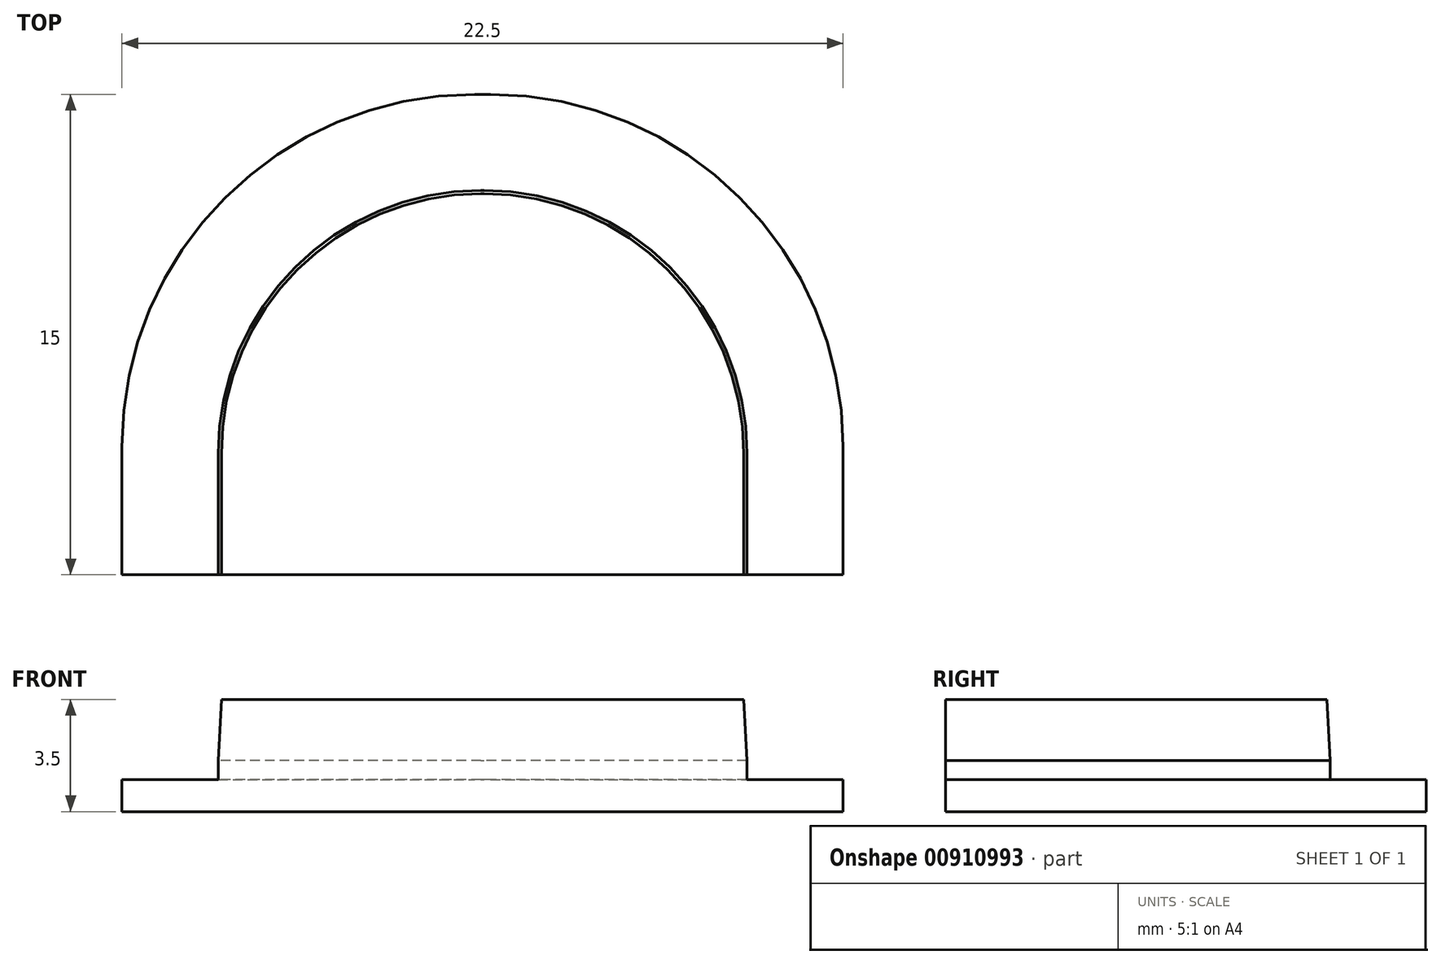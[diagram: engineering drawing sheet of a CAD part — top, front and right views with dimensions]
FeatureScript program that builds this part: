
annotation { "Feature Type Name" : "Feature", "Feature Type Description" : "" }
export const myFeature = defineFeature(function(context is Context, id is Id, definition is map)
    precondition{}
    {
        {
            var Q0;
            Q0=qCreatedBy(makeId("Top.planeOp"),FACE);
            var sketch = newSketch(context, id + "F0", { "sketchPlane" : qUnion([Q0])});
            skLineSegment(sketch, "E0.bottom", {"start": v(0, 0) * mm, "end": v(16.5, 0) * mm});
            skLineSegment(sketch, "E0.top", {"start": v(0, -12) * mm, "end": v(16.5, -12) * mm});
            skLineSegment(sketch, "E0.left", {"start": v(0, 0) * mm, "end": v(0, -12) * mm});
            skLineSegment(sketch, "E0.right", {"start": v(16.5, 0) * mm, "end": v(16.5, -12) * mm});
            skSolve(sketch);
        }
        {
            var Q0;
            Q0 = qSketchRegion(id + "F0", true);
            extrude(context, id + "F1", {"entities" : qUnion([Q0]), "depth" : 2.5 * mm, "offsetDistance" : 25 * mm});
        }
        {
            var Q0;
            Q0=makeQuery(id+"F1.opExtrude","SWEPT_EDGE",EDGE,{"disambiguationData":[OSD([sQuery(id+"F0.wireOp",EDGE,"E0.bottom"),sQuery(id+"F0.wireOp",EDGE,"E0.right")])]});
            var Q1;
            Q1=makeQuery(id+"F1.opExtrude","SWEPT_EDGE",EDGE,{"disambiguationData":[OSD([sQuery(id+"F0.wireOp",EDGE,"E0.bottom"),sQuery(id+"F0.wireOp",EDGE,"E0.left")])]});
            fillet(context, id + "F2", {"entities" : qUnion([Q0, Q1]), "radius" : 8.2 * mm, "tangentPropagation" : true, "allowEdgeOverflow" : false});
        }
        {
            var Q0;
            Q0=makeQuery(id+"F1.opExtrude","CAP_FACE",FACE,{"disambiguationData":[OSD([sQuery(id+"F0.wireOp",EDGE,"E0.bottom"),sQuery(id+"F0.wireOp",EDGE,"E0.top"),sQuery(id+"F0.wireOp",EDGE,"E0.left"),sQuery(id+"F0.wireOp",EDGE,"E0.right")])],"isStart":true});
            var sketch = newSketch(context, id + "F3", { "sketchPlane" : qUnion([Q0])});
            skLineSegment(sketch, "E1.bottom", {"start": v(19.5, 12) * mm, "end": v(-3, 12) * mm});
            skLineSegment(sketch, "E1.top", {"start": v(19.5, -3) * mm, "end": v(-3, -3) * mm});
            skLineSegment(sketch, "E1.left", {"start": v(19.5, 12) * mm, "end": v(19.5, -3) * mm});
            skLineSegment(sketch, "E1.right", {"start": v(-3, 12) * mm, "end": v(-3, -3) * mm});
            skSolve(sketch);
        }
        {
            var Q0;
            Q0 = qSketchRegion(id + "F3", true);
            extrude(context, id + "F4", {"entities" : qUnion([Q0]), "operationType" : NewBodyOperationType.ADD, "depth" : 1 * mm, "offsetDistance" : 25 * mm});
        }
        {
            var Q0;
            Q0=makeQuery(id+"F4.opExtrude","SWEPT_EDGE",EDGE,{"disambiguationData":[OSD([sQuery(id+"F3.wireOp",EDGE,"E1.top"),sQuery(id+"F3.wireOp",EDGE,"E1.left")])]});
            var Q1;
            Q1=makeQuery(id+"F4.opExtrude","SWEPT_EDGE",EDGE,{"disambiguationData":[OSD([sQuery(id+"F3.wireOp",EDGE,"E1.top"),sQuery(id+"F3.wireOp",EDGE,"E1.right")])]});
            fillet(context, id + "F5", {"entities" : qUnion([Q0, Q1]), "radius" : 11 * mm, "tangentPropagation" : true, "allowEdgeOverflow" : false});
        }
        {
            var Q0;
            Q0=makeQuery(id+"F1.opExtrude","CAP_EDGE",EDGE,{"disambiguationData":[OSD([sQuery(id+"F0.wireOp",EDGE,"E0.left")])],"isStart":false});
            var Q1;
            {var subQ0=sQuery(id+"F0.wireOp",EDGE,"E0.left");var subQ1=sQuery(id+"F0.wireOp",EDGE,"E0.bottom");Q1=makeQuery(id+"F2.opFillet","BLEND_EDGE",EDGE,{"blendedFrom":[makeQuery(id+"F1.opExtrude","SWEPT_EDGE",EDGE,{"disambiguationData":[OSD([subQ1,subQ0])]}),makeQuery(id+"F1.opExtrude","CAP_FACE",FACE,{"disambiguationData":[OSD([subQ1,sQuery(id+"F0.wireOp",EDGE,"E0.top"),subQ0,sQuery(id+"F0.wireOp",EDGE,"E0.right")])],"isStart":false})],"blendedInto":[makeQuery(id+"F1.opExtrude","CAP_FACE",FACE,{"disambiguationData":[OSD([subQ1,sQuery(id+"F0.wireOp",EDGE,"E0.top"),subQ0,sQuery(id+"F0.wireOp",EDGE,"E0.right")])],"isStart":false})]});}
            var Q2;
            {var subQ0=sQuery(id+"F0.wireOp",EDGE,"E0.right");var subQ1=sQuery(id+"F0.wireOp",EDGE,"E0.bottom");Q2=makeQuery(id+"F2.opFillet","BLEND_EDGE",EDGE,{"blendedFrom":[makeQuery(id+"F1.opExtrude","SWEPT_EDGE",EDGE,{"disambiguationData":[OSD([subQ1,subQ0])]}),makeQuery(id+"F1.opExtrude","CAP_FACE",FACE,{"disambiguationData":[OSD([subQ1,sQuery(id+"F0.wireOp",EDGE,"E0.top"),sQuery(id+"F0.wireOp",EDGE,"E0.left"),subQ0])],"isStart":false})],"blendedInto":[makeQuery(id+"F1.opExtrude","CAP_FACE",FACE,{"disambiguationData":[OSD([subQ1,sQuery(id+"F0.wireOp",EDGE,"E0.top"),sQuery(id+"F0.wireOp",EDGE,"E0.left"),subQ0])],"isStart":false})]});}
            var Q3;
            Q3=makeQuery(id+"F1.opExtrude","CAP_EDGE",EDGE,{"disambiguationData":[OSD([sQuery(id+"F0.wireOp",EDGE,"E0.right")])],"isStart":false});
            chamfer(context, id + "F6", {"entities" : qUnion([Q0, Q1, Q2, Q3]), "chamferType" : ChamferType.OFFSET_ANGLE, "width" : .1 * mm, "oppositeDirection" : false, "angle" : 87 * degree, "tangentPropagation" : true});
        }
    });
